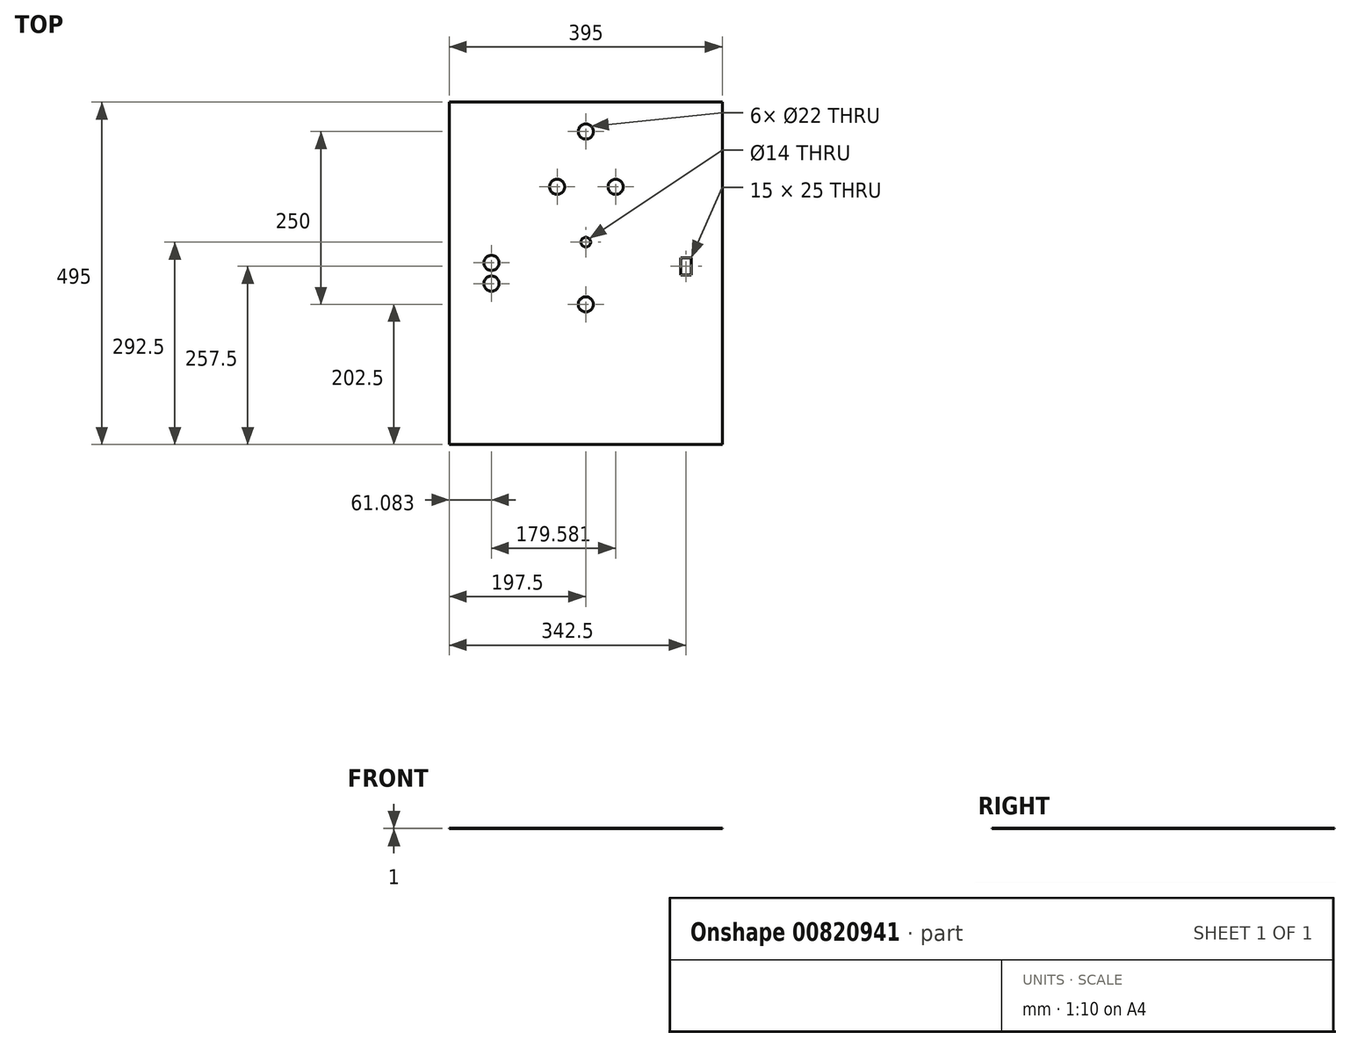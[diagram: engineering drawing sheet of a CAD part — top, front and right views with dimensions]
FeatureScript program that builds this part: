
annotation { "Feature Type Name" : "Feature", "Feature Type Description" : "" }
export const myFeature = defineFeature(function(context is Context, id is Id, definition is map)
    precondition{}
    {
        {
            var Q0;
            Q0=qCreatedBy(makeId("Top.planeOp"),FACE);
            var sketch = newSketch(context, id + "F0", { "sketchPlane" : qUnion([Q0])});
            skLineSegment(sketch, "E0.bottom", {"start": v(197.5, 247.5) * mm, "end": v(-197.5, 247.5) * mm});
            skLineSegment(sketch, "E0.top", {"start": v(197.5, -247.5) * mm, "end": v(-197.5, -247.5) * mm});
            skLineSegment(sketch, "E0.left", {"start": v(197.5, 247.5) * mm, "end": v(197.5, -247.5) * mm});
            skLineSegment(sketch, "E0.right", {"start": v(-197.5, 247.5) * mm, "end": v(-197.5, -247.5) * mm});
            skPoint(sketch, "E0.middle", {"position": v(0, 0) * mm});
            skLineSegment(sketch, "E1.bottom", {"start": v(137.5, 22.5) * mm, "end": v(152.5, 22.5) * mm});
            skLineSegment(sketch, "E1.top", {"start": v(137.5, -2.5) * mm, "end": v(152.5, -2.5) * mm});
            skLineSegment(sketch, "E1.left", {"start": v(137.5, 22.5) * mm, "end": v(137.5, -2.5) * mm});
            skLineSegment(sketch, "E1.right", {"start": v(152.5, 22.5) * mm, "end": v(152.5, -2.5) * mm});
            skCircle(sketch, "E2", {"center": v(0, 205) * mm, "radius": 11 * mm});
            skCircle(sketch, "E3", {"center": v(43.16, 125) * mm, "radius": 11 * mm});
            skCircle(sketch, "E4", {"center": v(-41.49, 125) * mm, "radius": 11 * mm});
            skCircle(sketch, "E5", {"center": v(-136.42, 15) * mm, "radius": 11 * mm});
            skCircle(sketch, "E6", {"center": v(-136.42, -15) * mm, "radius": 11 * mm});
            skCircle(sketch, "E7", {"center": v(0, 45) * mm, "radius": 7 * mm});
            skCircle(sketch, "E8", {"center": v(0, -45) * mm, "radius": 11 * mm});
            skSolve(sketch);
        }
        {
            var Q0;
            Q0 = qSketchRegion(id + "F0", true);
            extrude(context, id + "F1", {"entities" : qUnion([Q0]), "depth" : 1 * mm, "offsetDistance" : 25 * mm});
        }
    });
